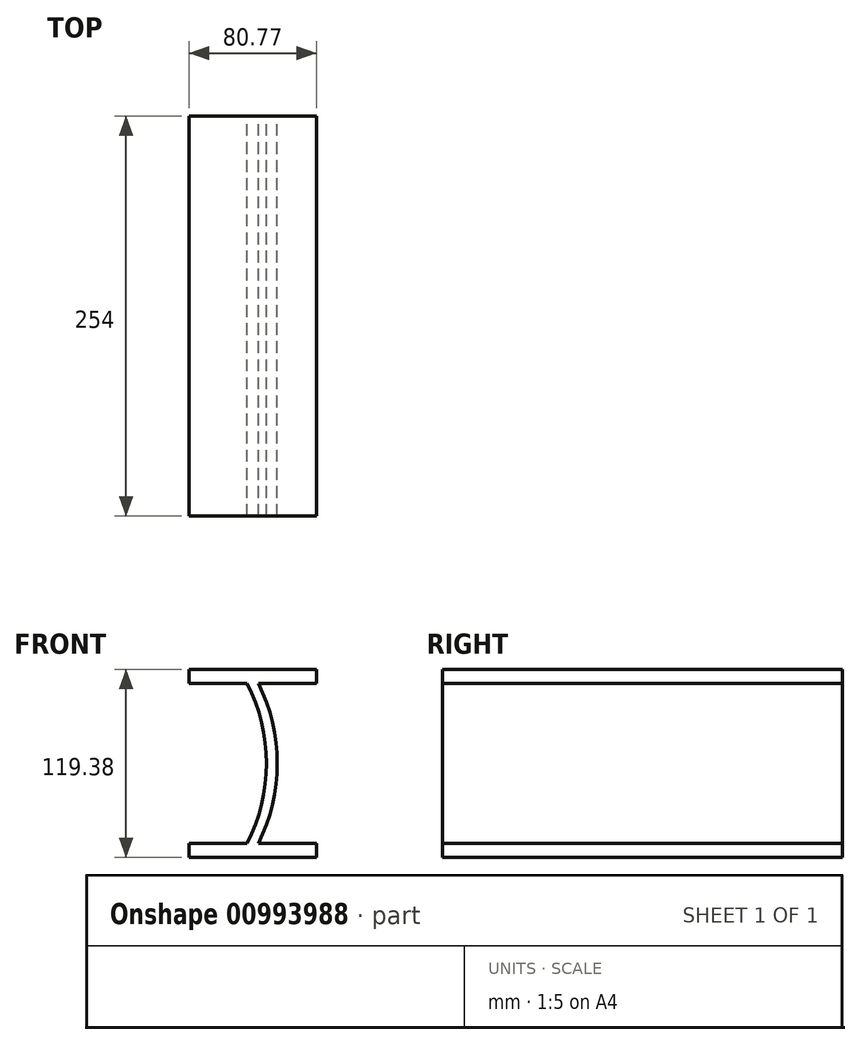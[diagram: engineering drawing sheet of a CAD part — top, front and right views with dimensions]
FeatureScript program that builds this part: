
annotation { "Feature Type Name" : "Feature", "Feature Type Description" : "" }
export const myFeature = defineFeature(function(context is Context, id is Id, definition is map)
    precondition{}
    {
        {
            var Q0;
            Q0=qCreatedBy(makeId("Front.planeOp"),FACE);
            var sketch = newSketch(context, id + "F0", { "sketchPlane" : qUnion([Q0])});
            skLineSegment(sketch, "E0.top", {"start": v(-3.1, 34.1) * mm, "end": v(-3.26, 34.1) * mm});
            skPoint(sketch, "E0.middle", {"position": v(0, 0) * mm});
            skLineSegment(sketch, "E1.bottom", {"start": v(-43.9, 42.86) * mm, "end": v(36.87, 42.86) * mm});
            skLineSegment(sketch, "E1.top", {"start": v(-43.9, 34.1) * mm, "end": v(-7.07, 34.1) * mm});
            skLineSegment(sketch, "E1.left", {"start": v(-43.9, 42.86) * mm, "end": v(-43.9, 34.1) * mm});
            skLineSegment(sketch, "E1.right", {"start": v(36.87, 42.86) * mm, "end": v(36.87, 34.1) * mm});
            skLineSegment(sketch, "E2.bottom", {"start": v(-43.9, -67.75) * mm, "end": v(-7.07, -67.75) * mm});
            skLineSegment(sketch, "E2.top", {"start": v(-43.9, -76.52) * mm, "end": v(36.87, -76.52) * mm});
            skLineSegment(sketch, "E2.left", {"start": v(-43.9, -67.75) * mm, "end": v(-43.9, -76.52) * mm});
            skLineSegment(sketch, "E2.right", {"start": v(36.87, -67.75) * mm, "end": v(36.87, -76.52) * mm});
            skPoint(sketch, "E3.newPointA", {"position": v(42.94, 34.1) * mm});
            skLineSegment(sketch, "E4", {"start": v(36.87, 34.1) * mm, "end": v(0.04, 34.1) * mm});
            skLineSegment(sketch, "E5", {"start": v(0.04, -67.75) * mm, "end": v(36.87, -67.75) * mm});
            skArc(sketch, "E6", {"start": v(-7.07, -67.75) * mm, "mid": v(5.2, -16.83) * mm, "end": v(-7.07, 34.1) * mm});
            skArc(sketch, "E7", {"start": v(0.04, -67.75) * mm, "mid": v(11.94, -16.83) * mm, "end": v(0.04, 34.1) * mm});
            skSolve(sketch);
        }
        {
            var Q0;
            Q0=qSketchRegion(id+"F0",true);
            extrude(context, id + "F1", {"entities" : qUnion([Q0]), "depth" : 254 * mm, "offsetDistance" : 25.4 * mm});
        }
    });
